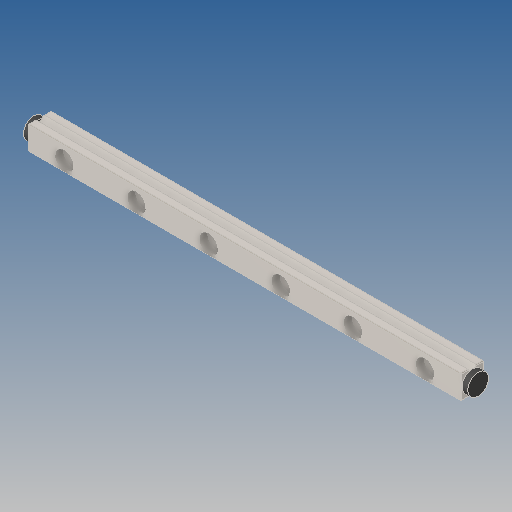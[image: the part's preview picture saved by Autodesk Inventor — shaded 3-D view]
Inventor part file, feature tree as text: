
AUTODESK INVENTOR PART (.ipt)
format: ipt  version: 2019 (Build 230136000, 136)  size: 136,192 bytes
history: native  units: mm
features: chamfer x1
ambient origin geometry x8: Origin, YZ Plane, XZ Plane, XY Plane, X Axis, Y Axis, Z Axis, Center Point
bodies: Solid1 (feature_tree)
feature tree (1):
  chamfer  "Chamfer1"  [1 undecoded]
note: 1 required parameter value undecoded (feature->parameter linkage not recoverable at this tier; creation-order binding heuristic only, values carry confidence <= 0.55)
